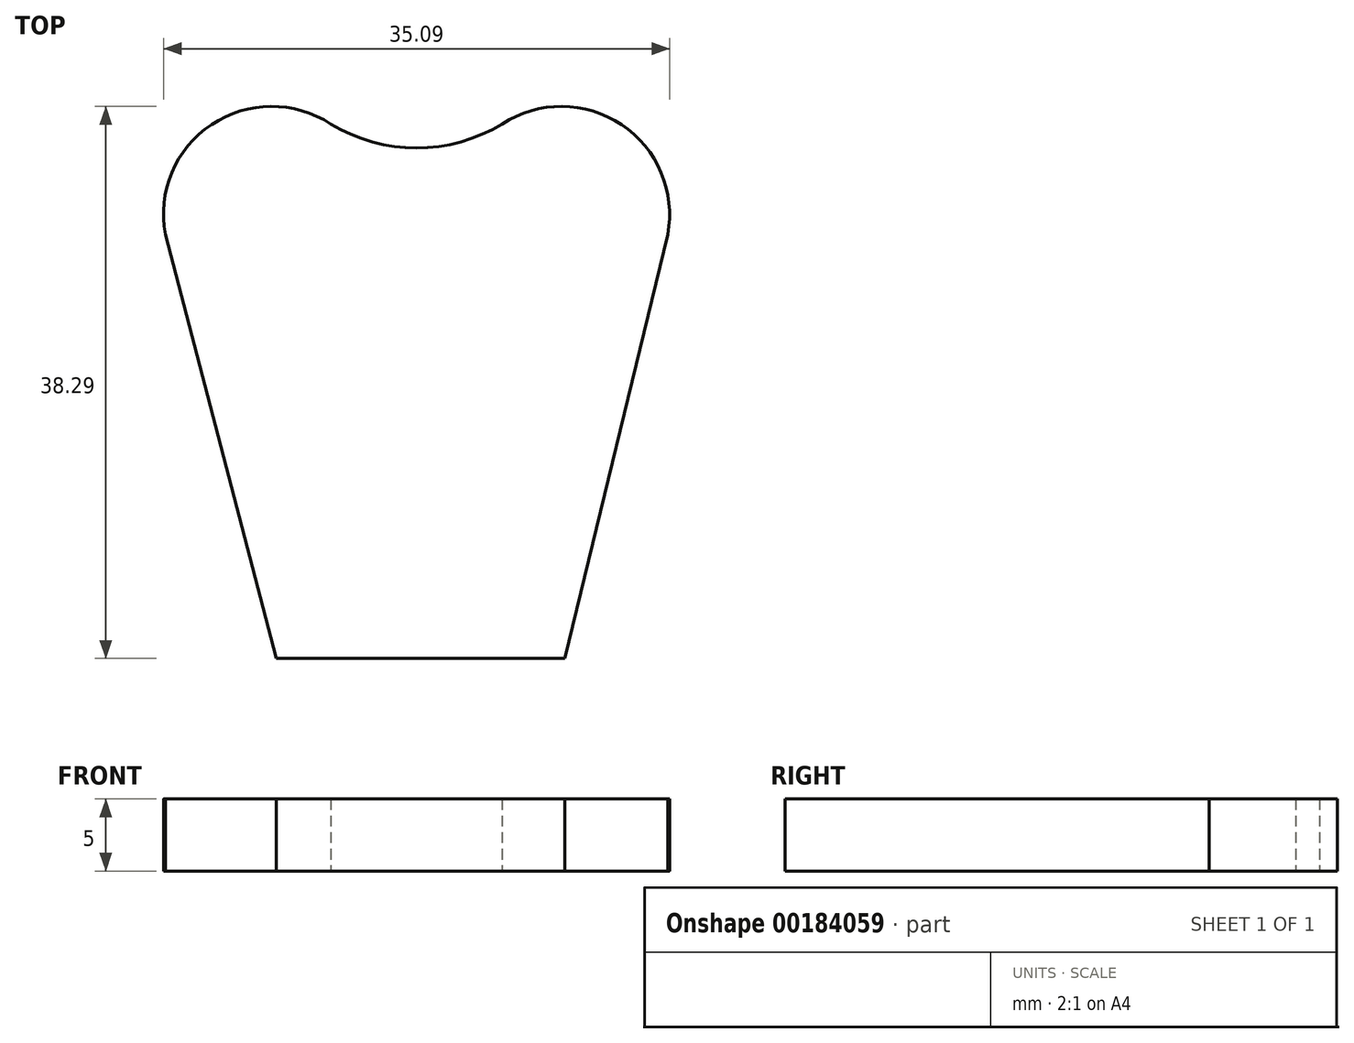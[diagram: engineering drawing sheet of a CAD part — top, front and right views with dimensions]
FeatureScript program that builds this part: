
annotation { "Feature Type Name" : "Feature", "Feature Type Description" : "" }
export const myFeature = defineFeature(function(context is Context, id is Id, definition is map)
    precondition{}
    {
        {
            var Q0;
            Q0=qCreatedBy(makeId("Top.planeOp"),FACE);
            var sketch = newSketch(context, id + "F0", { "sketchPlane" : qUnion([Q0])});
            skArc(sketch, "E0", {"start": v(-19.42, 65.67) * mm, "mid": v(-28.12, 65.32) * mm, "end": v(-30.63, 56.99) * mm});
            skArc(sketch, "E1", {"start": v(3.75, 57.25) * mm, "mid": v(1.06, 65.4) * mm, "end": v(-7.53, 65.67) * mm});
            skLineSegment(sketch, "E2", {"start": v(-13.2, 28.6) * mm, "end": v(-3.2, 28.6) * mm});
            skLineSegment(sketch, "E3", {"start": v(-13.2, 28.6) * mm, "end": v(-23.2, 28.6) * mm});
            skLineSegment(sketch, "E4", {"start": v(3.94, 58.01) * mm, "end": v(-3.2, 28.6) * mm});
            skLineSegment(sketch, "E5", {"start": v(-30.9, 58.01) * mm, "end": v(-23.2, 28.6) * mm});
            skArc(sketch, "E6", {"start": v(-19.42, 65.67) * mm, "mid": v(-13.48, 64.01) * mm, "end": v(-7.53, 65.67) * mm});
            skPoint(sketch, "E6.endSnap0", {"position": v(-19.42, 65.67) * mm});
            skSolve(sketch);
        }
        {
            var Q0;
            {var subQ1=sQuery(id+"F0.wireOp",EDGE,"E2");Q0=makeQuery(id+"F0.imprint","IMPRINT",FACE,{"disambiguationData":[TD([[makeQuery(id+"F0.imprint","IMPRINT",EDGE,{"derivedFrom":subQ1}),1.0]])]});}
            extrude(context, id + "F1", {"entities" : qUnion([Q0]), "depth" : 5 * mm});
        }
    });
